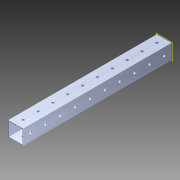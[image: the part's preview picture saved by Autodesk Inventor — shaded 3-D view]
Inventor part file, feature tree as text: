
AUTODESK INVENTOR PART (.ipt)
format: ipt  version: 2014 (Build 180170000, 170)  size: 1,229,824 bytes
history: native  units: in
note: dims shown in document units (in); Inventor stores cm internally (conversion verified against a paired STEP export)
features: extrude x3, sketch x3, pattern_circular x1, other x1, plane x1, imported_body x1
ambient origin geometry x8: Origin, YZ Plane, XZ Plane, XY Plane, X Axis, Y Axis, Z Axis, Center Point
bodies: Body1 (feature_tree)
feature tree (10):
  pattern_circular  "CirPattern2"
  other  "217-3426-STEP1"
  plane  "Work Plane1"
  extrude  "Extrusion1"  Depth=3937.0079in TaperAngle=0.0deg
  extrude  "Extrusion2"  Depth=10.0in TaperAngle=0.0deg
  extrude  "Extrusion3"  [1 undecoded]
  imported_body  "Base1"
  sketch  "Sketch1"  dims[d0=-21.0in d1=3937.0079in d2=0.0in]
  sketch  "Sketch3"  dims[d3=1.0in d4=0.0in d5=10.0in d6=0.0in]
  sketch  "Sketch4"
note: 1 required parameter value undecoded (feature->parameter linkage not recoverable at this tier; creation-order binding heuristic only, values carry confidence <= 0.55)
